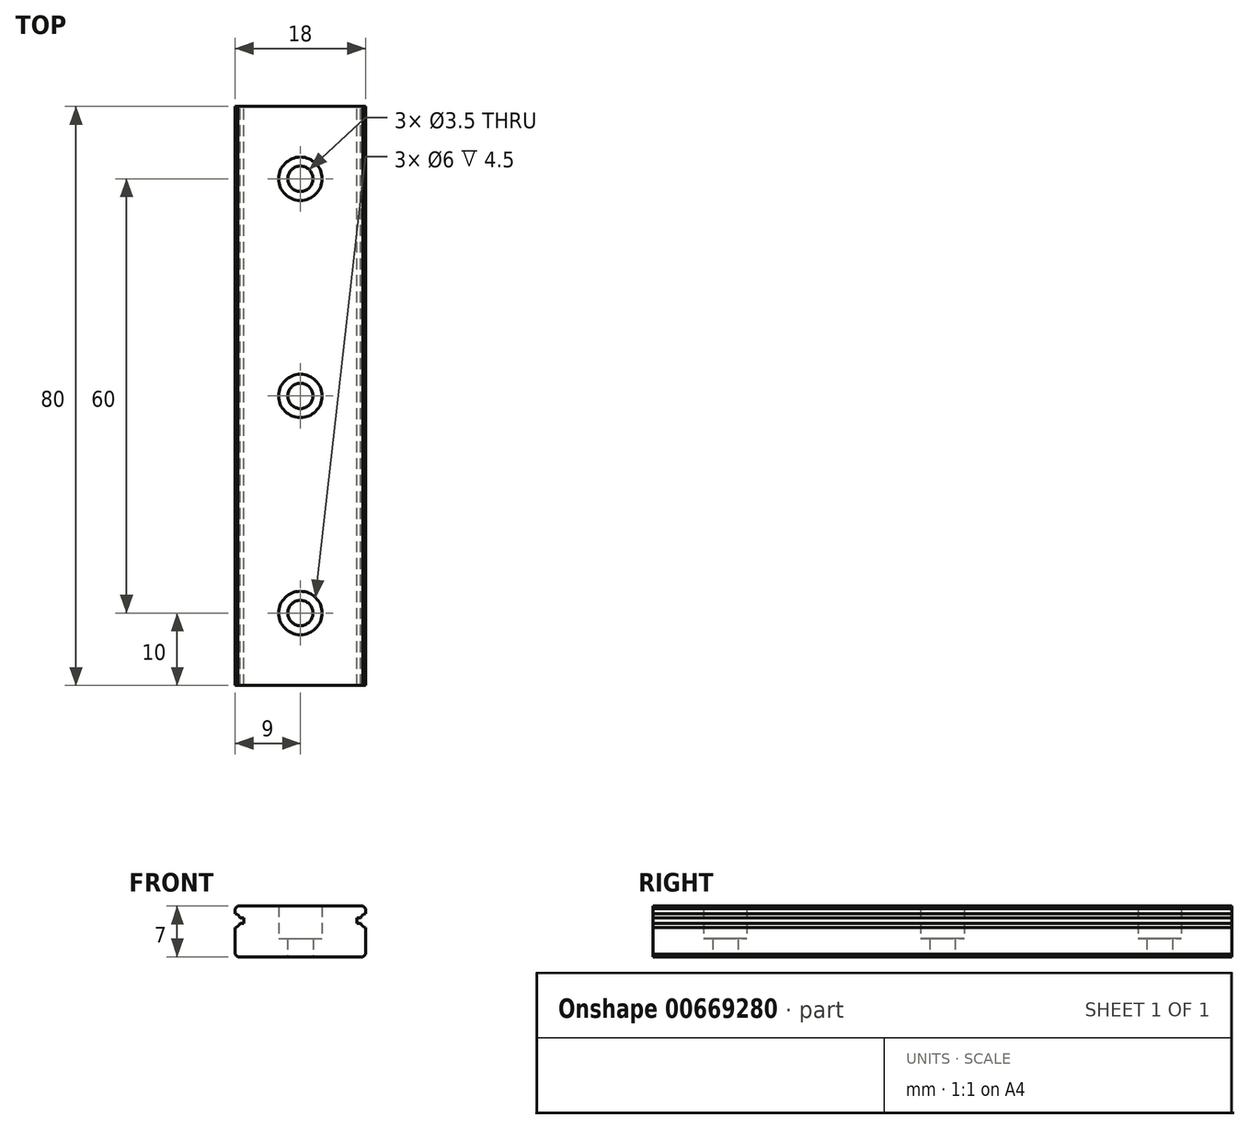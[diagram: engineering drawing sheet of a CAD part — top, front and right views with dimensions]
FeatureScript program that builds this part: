
annotation { "Feature Type Name" : "Feature", "Feature Type Description" : "" }
export const myFeature = defineFeature(function(context is Context, id is Id, definition is map)
    precondition{}
    {
        {
            assignVariable(context, id + "F0", {"variableType" : VariableType.LENGTH, "name" : "D", "lengthValue" : 6 * mm});
        }
        {
            assignVariable(context, id + "F1", {"variableType" : VariableType.LENGTH, "name" : "d", "lengthValue" : 3.5 * mm});
        }
        {
            assignVariable(context, id + "F2", {"variableType" : VariableType.LENGTH, "name" : "h", "lengthValue" : 4.5 * mm});
        }
        {
            var Q0;
            Q0=qCreatedBy(makeId("Front.planeOp"),FACE);
            var sketch = newSketch(context, id + "F3", { "sketchPlane" : qUnion([Q0])});
            skLineSegment(sketch, "E0.bottom", {"start": v(0, -3.5) * mm, "end": v(-8.65, -3.5) * mm});
            skLineSegment(sketch, "E0.right", {"start": v(-9, -3.15) * mm, "end": v(-9, 0.53) * mm});
            skArc(sketch, "E1", {"start": v(-9, 0.53) * mm, "mid": v(-8.6, 0.74) * mm, "end": v(-8.33, 1.1) * mm});
            skLineSegment(sketch, "E2", {"start": v(-7.8, 1.1) * mm, "end": v(-8.33, 1.1) * mm});
            skLineSegment(sketch, "E3", {"start": v(-7.8, 1.9) * mm, "end": v(-8.33, 1.9) * mm});
            skLineSegment(sketch, "E4", {"start": v(-9, 3.15) * mm, "end": v(-8.65, 3.5) * mm});
            skLineSegment(sketch, "E5.MirrorCS", {"start": v(-9, -3.15) * mm, "end": v(-8.65, -3.5) * mm});
            skPoint(sketch, "E6.orphan", {"position": v(-9, 3.5) * mm});
            skLineSegment(sketch, "E7.trimOffspring", {"start": v(-9, 2.47) * mm, "end": v(-9, 3.15) * mm});
            skArc(sketch, "E8.trimOffspring", {"start": v(-8.33, 1.9) * mm, "mid": v(-8.6, 2.26) * mm, "end": v(-9, 2.47) * mm});
            skPoint(sketch, "E9.orphan", {"position": v(-9, -3.5) * mm});
            skLineSegment(sketch, "E10", {"start": v(-8.65, 3.5) * mm, "end": v(0, 3.5) * mm});
            skLineSegment(sketch, "E11", {"start": v(-7.8, 1.9) * mm, "end": v(-7.8, 1.1) * mm});
            skLineSegment(sketch, "E12", {"start": v(-9.25, 1.5) * mm, "end": v(0, 1.5) * mm, "construction": true});
            skLineSegment(sketch, "E13.MirrorCS", {"start": v(9, 3.15) * mm, "end": v(8.65, 3.5) * mm});
            skLineSegment(sketch, "E14.MirrorCS", {"start": v(9, -3.15) * mm, "end": v(8.65, -3.5) * mm});
            skLineSegment(sketch, "E15.MirrorCS", {"start": v(7.8, 1.9) * mm, "end": v(7.8, 1.1) * mm});
            skLineSegment(sketch, "E16.MirrorCS", {"start": v(9, 2.47) * mm, "end": v(9, 3.15) * mm});
            skPoint(sketch, "E17.MirrorP", {"position": v(9, 3.5) * mm});
            skPoint(sketch, "E18.MirrorP", {"position": v(9, -3.5) * mm});
            skLineSegment(sketch, "E19.MirrorCS", {"start": v(9, -3.15) * mm, "end": v(9, 0.53) * mm});
            skArc(sketch, "E20.MirrorCS", {"start": v(9, 0.53) * mm, "mid": v(8.6, 0.74) * mm, "end": v(8.33, 1.1) * mm});
            skLineSegment(sketch, "E21.MirrorCS", {"start": v(7.8, 1.1) * mm, "end": v(8.33, 1.1) * mm});
            skLineSegment(sketch, "E22.MirrorCS", {"start": v(7.8, 1.9) * mm, "end": v(8.33, 1.9) * mm});
            skArc(sketch, "E23.MirrorCS", {"start": v(8.33, 1.9) * mm, "mid": v(8.6, 2.26) * mm, "end": v(9, 2.47) * mm});
            skLineSegment(sketch, "E24.MirrorCS", {"start": v(8.65, 3.5) * mm, "end": v(0, 3.5) * mm});
            skLineSegment(sketch, "E25.MirrorCS", {"start": v(0, -3.5) * mm, "end": v(8.65, -3.5) * mm});
            skSolve(sketch);
        }
        {
            var Q0;
            Q0=makeQuery(id+"F3.imprint","IMPRINT",FACE,{"disambiguationData":[TD([[makeQuery(id+"F3.imprint","IMPRINT",EDGE,{"derivedFrom":sQuery(id+"F3.wireOp",EDGE,"E0.bottom")}),-1.0]])]});
            extrude(context, id + "F4", {"entities" : qUnion([Q0]), "depth" : 80 * mm, "offsetDistance" : 25 * mm});
        }
        {
            var Q0;
            Q0=makeQuery(id+"F4.opExtrude","SWEPT_FACE",FACE,{"disambiguationData":[OSD([sQuery(id+"F3.wireOp",EDGE,"E10"),sQuery(id+"F3.wireOp",EDGE,"E24.MirrorCS")])]});
            var sketch = newSketch(context, id + "F5", { "sketchPlane" : qUnion([Q0])});
            skPoint(sketch, "E26", {"position": v(0, -10) * mm});
            skPoint(sketch, "E27.1.0.0", {"position": v(0, -40) * mm});
            skPoint(sketch, "E27.2.0.0", {"position": v(0, -70) * mm});
            skPoint(sketch, "E27.3.0.0", {"position": v(0, -100) * mm});
            skPoint(sketch, "E27.4.0.0", {"position": v(0, -130) * mm});
            skPoint(sketch, "E27.5.0.0", {"position": v(0, -160) * mm});
            skPoint(sketch, "E27.6.0.0", {"position": v(0, -190) * mm});
            skPoint(sketch, "E27.7.0.0", {"position": v(0, -220) * mm});
            skPoint(sketch, "E27.8.0.0", {"position": v(0, -250) * mm});
            skPoint(sketch, "E27.9.0.0", {"position": v(0, -280) * mm});
            skPoint(sketch, "E27.10.0.0", {"position": v(0, -310) * mm});
            skPoint(sketch, "E27.11.0.0", {"position": v(0, -340) * mm});
            skPoint(sketch, "E27.12.0.0", {"position": v(0, -370) * mm});
            skPoint(sketch, "E27.13.0.0", {"position": v(0, -400) * mm});
            skPoint(sketch, "E27.14.0.0", {"position": v(0, -430) * mm});
            skPoint(sketch, "E27.15.0.0", {"position": v(0, -460) * mm});
            skPoint(sketch, "E27.16.0.0", {"position": v(0, -490) * mm});
            skPoint(sketch, "E27.17.0.0", {"position": v(0, -520) * mm});
            skPoint(sketch, "E27.18.0.0", {"position": v(0, -550) * mm});
            skPoint(sketch, "E27.19.0.0", {"position": v(0, -580) * mm});
            skPoint(sketch, "E27.20.0.0", {"position": v(0, -610) * mm});
            skPoint(sketch, "E27.21.0.0", {"position": v(0, -640) * mm});
            skPoint(sketch, "E27.22.0.0", {"position": v(0, -670) * mm});
            skPoint(sketch, "E27.23.0.0", {"position": v(0, -700) * mm});
            skPoint(sketch, "E27.24.0.0", {"position": v(0, -730) * mm});
            skPoint(sketch, "E27.25.0.0", {"position": v(0, -760) * mm});
            skPoint(sketch, "E27.26.0.0", {"position": v(0, -790) * mm});
            skPoint(sketch, "E27.27.0.0", {"position": v(0, -820) * mm});
            skPoint(sketch, "E27.28.0.0", {"position": v(0, -850) * mm});
            skPoint(sketch, "E27.29.0.0", {"position": v(0, -880) * mm});
            skPoint(sketch, "E27.30.0.0", {"position": v(0, -910) * mm});
            skPoint(sketch, "E27.31.0.0", {"position": v(0, -940) * mm});
            skPoint(sketch, "E27.32.0.0", {"position": v(0, -970) * mm});
            skPoint(sketch, "E27.33.0.0", {"position": v(0, -1000) * mm});
            skPoint(sketch, "E27.34.0.0", {"position": v(0, -1030) * mm});
            skPoint(sketch, "E27.35.0.0", {"position": v(0, -1060) * mm});
            skPoint(sketch, "E27.36.0.0", {"position": v(0, -1090) * mm});
            skPoint(sketch, "E27.37.0.0", {"position": v(0, -1120) * mm});
            skPoint(sketch, "E27.38.0.0", {"position": v(0, -1150) * mm});
            skPoint(sketch, "E27.39.0.0", {"position": v(0, -1180) * mm});
            skLineSegment(sketch, "E27.direction1", {"start": v(0, -10) * mm, "end": v(0, -40) * mm, "construction": true});
            skPoint(sketch, "E28.0.40.0", {"position": v(0, -1210) * mm});
            skPoint(sketch, "E28.0.41.0", {"position": v(0, -1240) * mm});
            skPoint(sketch, "E28.0.42.0", {"position": v(0, -1270) * mm});
            skPoint(sketch, "E28.0.43.0", {"position": v(0, -1300) * mm});
            skPoint(sketch, "E28.0.44.0", {"position": v(0, -1330) * mm});
            skPoint(sketch, "E28.0.45.0", {"position": v(0, -1360) * mm});
            skPoint(sketch, "E28.0.46.0", {"position": v(0, -1390) * mm});
            skPoint(sketch, "E28.0.47.0", {"position": v(0, -1420) * mm});
            skPoint(sketch, "E28.0.48.0", {"position": v(0, -1450) * mm});
            skPoint(sketch, "E28.0.49.0", {"position": v(0, -1480) * mm});
            skPoint(sketch, "E28.0.50.0", {"position": v(0, -1510) * mm});
            skPoint(sketch, "E28.0.51.0", {"position": v(0, -1540) * mm});
            skPoint(sketch, "E28.0.52.0", {"position": v(0, -1570) * mm});
            skPoint(sketch, "E28.0.53.0", {"position": v(0, -1600) * mm});
            skPoint(sketch, "E28.0.54.0", {"position": v(0, -1630) * mm});
            skPoint(sketch, "E28.0.55.0", {"position": v(0, -1660) * mm});
            skPoint(sketch, "E28.0.56.0", {"position": v(0, -1690) * mm});
            skPoint(sketch, "E28.0.57.0", {"position": v(0, -1720) * mm});
            skPoint(sketch, "E28.0.58.0", {"position": v(0, -1750) * mm});
            skPoint(sketch, "E28.0.59.0", {"position": v(0, -1780) * mm});
            skPoint(sketch, "E28.0.60.0", {"position": v(0, -1810) * mm});
            skPoint(sketch, "E28.0.61.0", {"position": v(0, -1840) * mm});
            skPoint(sketch, "E28.0.62.0", {"position": v(0, -1870) * mm});
            skPoint(sketch, "E28.0.63.0", {"position": v(0, -1900) * mm});
            skPoint(sketch, "E28.0.64.0", {"position": v(0, -1930) * mm});
            skPoint(sketch, "E28.0.65.0", {"position": v(0, -1960) * mm});
            skSolve(sketch);
        }
        {
            var Q0;
            Q0=sQuery(id+"F5.wireOp",VERTEX,"E27.15.0.0");
            var Q1;
            Q1=sQuery(id+"F5.wireOp",VERTEX,"E27.36.0.0");
            var Q2;
            Q2=sQuery(id+"F5.wireOp",VERTEX,"E27.26.0.0");
            var Q3;
            Q3=sQuery(id+"F5.wireOp",VERTEX,"E27.5.0.0");
            var Q4;
            Q4=sQuery(id+"F5.wireOp",VERTEX,"E27.19.0.0");
            var Q5;
            Q5=sQuery(id+"F5.wireOp",VERTEX,"E27.21.0.0");
            var Q6;
            Q6=sQuery(id+"F5.wireOp",VERTEX,"E27.6.0.0");
            var Q7;
            Q7=sQuery(id+"F5.wireOp",VERTEX,"E27.direction1.start");
            var Q8;
            Q8=sQuery(id+"F5.wireOp",VERTEX,"E27.4.0.0");
            var Q9;
            Q9=sQuery(id+"F5.wireOp",VERTEX,"E27.24.0.0");
            var Q10;
            Q10=sQuery(id+"F5.wireOp",VERTEX,"E27.3.0.0");
            var Q11;
            Q11=sQuery(id+"F5.wireOp",VERTEX,"E27.20.0.0");
            var Q12;
            Q12=sQuery(id+"F5.wireOp",VERTEX,"E27.1.0.0");
            var Q13;
            Q13=sQuery(id+"F5.wireOp",VERTEX,"E27.39.0.0");
            var Q14;
            Q14=sQuery(id+"F5.wireOp",VERTEX,"E27.11.0.0");
            var Q15;
            Q15=sQuery(id+"F5.wireOp",VERTEX,"E27.38.0.0");
            var Q16;
            Q16=sQuery(id+"F5.wireOp",VERTEX,"E27.37.0.0");
            var Q17;
            Q17=sQuery(id+"F5.wireOp",VERTEX,"E27.25.0.0");
            var Q18;
            Q18=sQuery(id+"F5.wireOp",VERTEX,"E27.31.0.0");
            var Q19;
            Q19=sQuery(id+"F5.wireOp",VERTEX,"E27.34.0.0");
            var Q20;
            Q20=sQuery(id+"F5.wireOp",VERTEX,"E27.23.0.0");
            var Q21;
            Q21=sQuery(id+"F5.wireOp",VERTEX,"E27.13.0.0");
            var Q22;
            Q22=sQuery(id+"F5.wireOp",VERTEX,"E27.18.0.0");
            var Q23;
            Q23=sQuery(id+"F5.wireOp",VERTEX,"E27.16.0.0");
            var Q24;
            Q24=sQuery(id+"F5.wireOp",VERTEX,"E27.30.0.0");
            var Q25;
            Q25=sQuery(id+"F5.wireOp",VERTEX,"E27.7.0.0");
            var Q26;
            Q26=sQuery(id+"F5.wireOp",VERTEX,"E27.22.0.0");
            var Q27;
            Q27=sQuery(id+"F5.wireOp",VERTEX,"E27.9.0.0");
            var Q28;
            Q28=sQuery(id+"F5.wireOp",VERTEX,"E27.32.0.0");
            var Q29;
            Q29=sQuery(id+"F5.wireOp",VERTEX,"E27.28.0.0");
            var Q30;
            Q30=sQuery(id+"F5.wireOp",VERTEX,"E27.10.0.0");
            var Q31;
            Q31=sQuery(id+"F5.wireOp",VERTEX,"E27.2.0.0");
            var Q32;
            Q32=sQuery(id+"F5.wireOp",VERTEX,"E27.35.0.0");
            var Q33;
            Q33=sQuery(id+"F5.wireOp",VERTEX,"E27.29.0.0");
            var Q34;
            Q34=sQuery(id+"F5.wireOp",VERTEX,"E27.33.0.0");
            var Q35;
            Q35=sQuery(id+"F5.wireOp",VERTEX,"E27.17.0.0");
            var Q36;
            Q36=sQuery(id+"F5.wireOp",VERTEX,"E27.8.0.0");
            var Q37;
            Q37=sQuery(id+"F5.wireOp",VERTEX,"E27.12.0.0");
            var Q38;
            Q38=sQuery(id+"F5.wireOp",VERTEX,"E27.27.0.0");
            var Q39;
            Q39=sQuery(id+"F5.wireOp",VERTEX,"E27.14.0.0");
            var Q40;
            Q40=sQuery(id+"F5.wireOp",VERTEX,"E28.0.47.0");
            var Q41;
            Q41=sQuery(id+"F5.wireOp",VERTEX,"E28.0.63.0");
            var Q42;
            Q42=sQuery(id+"F5.wireOp",VERTEX,"E28.0.48.0");
            var Q43;
            Q43=sQuery(id+"F5.wireOp",VERTEX,"E28.0.44.0");
            var Q44;
            Q44=sQuery(id+"F5.wireOp",VERTEX,"E28.0.50.0");
            var Q45;
            Q45=sQuery(id+"F5.wireOp",VERTEX,"E28.0.51.0");
            var Q46;
            Q46=sQuery(id+"F5.wireOp",VERTEX,"E28.0.64.0");
            var Q47;
            Q47=sQuery(id+"F5.wireOp",VERTEX,"E28.0.65.0");
            var Q48;
            Q48=sQuery(id+"F5.wireOp",VERTEX,"E28.0.49.0");
            var Q49;
            Q49=sQuery(id+"F5.wireOp",VERTEX,"E28.0.46.0");
            var Q50;
            Q50=sQuery(id+"F5.wireOp",VERTEX,"E28.0.62.0");
            var Q51;
            Q51=sQuery(id+"F5.wireOp",VERTEX,"E28.0.52.0");
            var Q52;
            Q52=sQuery(id+"F5.wireOp",VERTEX,"E28.0.45.0");
            var Q53;
            Q53=sQuery(id+"F5.wireOp",VERTEX,"E28.0.40.0");
            var Q54;
            Q54=sQuery(id+"F5.wireOp",VERTEX,"E28.0.60.0");
            var Q55;
            Q55=sQuery(id+"F5.wireOp",VERTEX,"E28.0.56.0");
            var Q56;
            Q56=sQuery(id+"F5.wireOp",VERTEX,"E28.0.61.0");
            var Q57;
            Q57=sQuery(id+"F5.wireOp",VERTEX,"E28.0.54.0");
            var Q58;
            Q58=sQuery(id+"F5.wireOp",VERTEX,"E28.0.41.0");
            var Q59;
            Q59=sQuery(id+"F5.wireOp",VERTEX,"E28.0.42.0");
            var Q60;
            Q60=sQuery(id+"F5.wireOp",VERTEX,"E28.0.53.0");
            var Q61;
            Q61=sQuery(id+"F5.wireOp",VERTEX,"E28.0.59.0");
            var Q62;
            Q62=sQuery(id+"F5.wireOp",VERTEX,"E28.0.43.0");
            var Q63;
            Q63=sQuery(id+"F5.wireOp",VERTEX,"E28.0.57.0");
            var Q64;
            Q64=sQuery(id+"F5.wireOp",VERTEX,"E28.0.58.0");
            var Q65;
            Q65=sQuery(id+"F5.wireOp",VERTEX,"E28.0.55.0");
            var Q66;
            Q66=makeQuery(id+"F4.opExtrude","SWEPT_BODY",BODY,{"disambiguationData":[OSD([sQuery(id+"F3.wireOp",EDGE,"E0.bottom"),sQuery(id+"F3.wireOp",EDGE,"E0.right"),sQuery(id+"F3.wireOp",EDGE,"E1"),sQuery(id+"F3.wireOp",EDGE,"E2"),sQuery(id+"F3.wireOp",EDGE,"E3"),sQuery(id+"F3.wireOp",EDGE,"E4"),sQuery(id+"F3.wireOp",EDGE,"E5.MirrorCS"),sQuery(id+"F3.wireOp",EDGE,"E7.trimOffspring"),sQuery(id+"F3.wireOp",EDGE,"E8.trimOffspring"),sQuery(id+"F3.wireOp",EDGE,"E10"),sQuery(id+"F3.wireOp",EDGE,"E11"),sQuery(id+"F3.wireOp",EDGE,"E13.MirrorCS"),sQuery(id+"F3.wireOp",EDGE,"E14.MirrorCS"),sQuery(id+"F3.wireOp",EDGE,"E15.MirrorCS"),sQuery(id+"F3.wireOp",EDGE,"E16.MirrorCS"),sQuery(id+"F3.wireOp",EDGE,"E19.MirrorCS"),sQuery(id+"F3.wireOp",EDGE,"E20.MirrorCS"),sQuery(id+"F3.wireOp",EDGE,"E21.MirrorCS"),sQuery(id+"F3.wireOp",EDGE,"E22.MirrorCS"),sQuery(id+"F3.wireOp",EDGE,"E23.MirrorCS"),sQuery(id+"F3.wireOp",EDGE,"E24.MirrorCS"),sQuery(id+"F3.wireOp",EDGE,"E25.MirrorCS")])]});
            hole(context, id + "F6", {"style" : HoleStyle.C_BORE, "endStyle" : HoleEndStyle.THROUGH, "holeDiameter" : getVariable(context, 'd'), "cBoreDiameter" : getVariable(context, 'D'), "cBoreDepth" : getVariable(context, 'h'), "majorDiameter" : 5 * mm, "isTappedThrough" : true, "tappedDepth" : 1 * mm, "tapClearance" : 3, "locations" : qUnion([Q0, Q1, Q2, Q3, Q4, Q5, Q6, Q7, Q8, Q9, Q10, Q11, Q12, Q13, Q14, Q15, Q16, Q17, Q18, Q19, Q20, Q21, Q22, Q23, Q24, Q25, Q26, Q27, Q28, Q29, Q30, Q31, Q32, Q33, Q34, Q35, Q36, Q37, Q38, Q39, Q40, Q41, Q42, Q43, Q44, Q45, Q46, Q47, Q48, Q49, Q50, Q51, Q52, Q53, Q54, Q55, Q56, Q57, Q58, Q59, Q60, Q61, Q62, Q63, Q64, Q65]), "scope" : qUnion([Q66]), "startStyle" : HoleStartStyle.PART});
        }
    });
